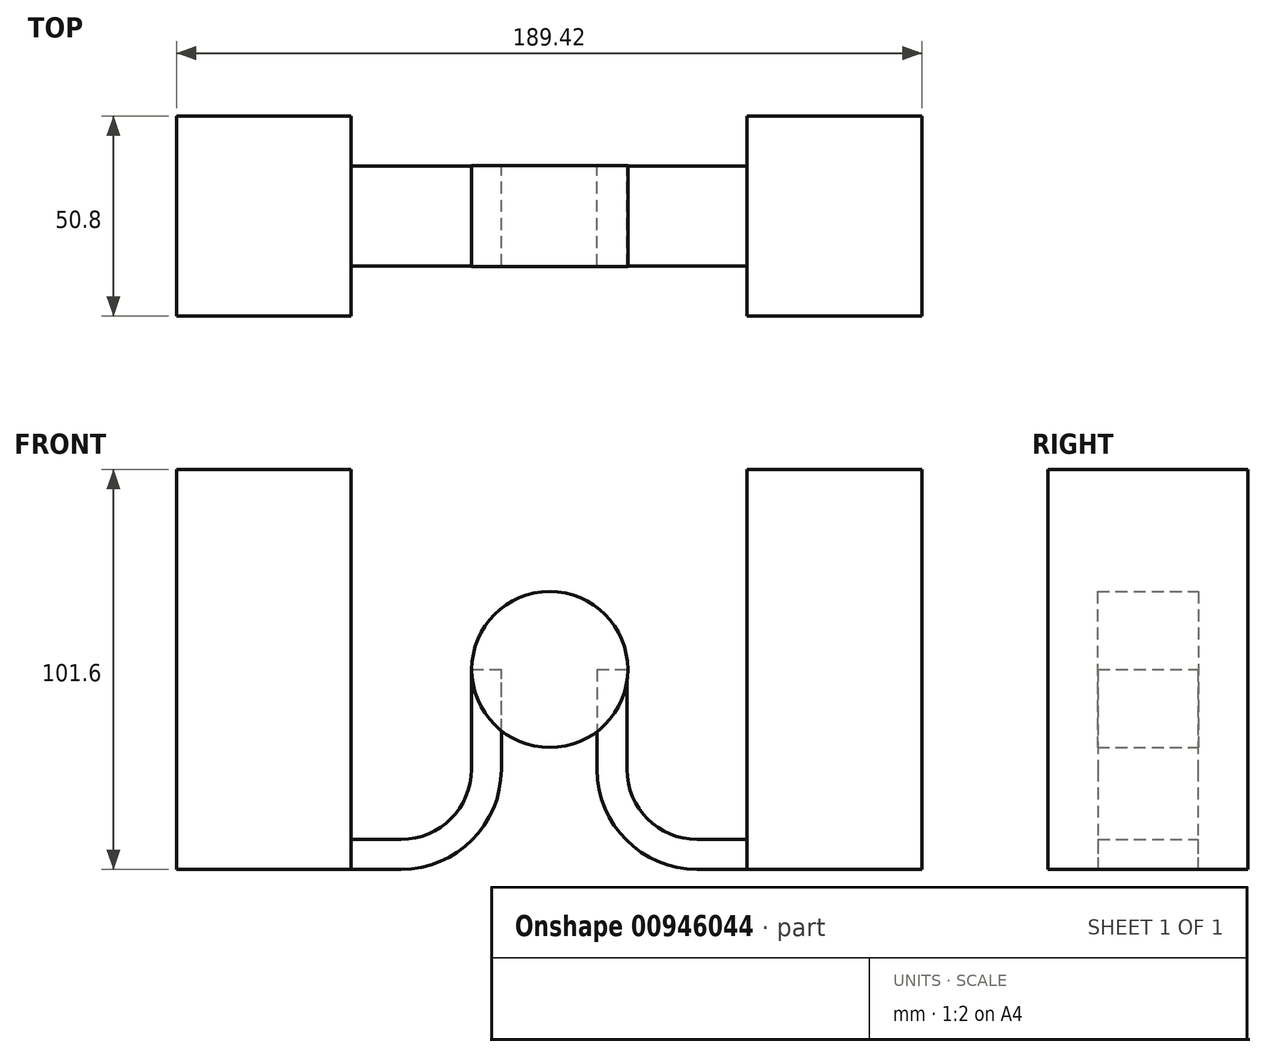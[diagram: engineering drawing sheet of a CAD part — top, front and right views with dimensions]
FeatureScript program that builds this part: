
annotation { "Feature Type Name" : "Feature", "Feature Type Description" : "" }
export const myFeature = defineFeature(function(context is Context, id is Id, definition is map)
    precondition{}
    {
        {
            var Q0;
            Q0=qCreatedBy(makeId("Front.planeOp"),FACE);
            var sketch = newSketch(context, id + "F0", { "sketchPlane" : qUnion([Q0])});
            skLineSegment(sketch, "E0.bottom", {"start": v(-94.87, 50.8) * mm, "end": v(-50.42, 50.8) * mm});
            skLineSegment(sketch, "E0.top", {"start": v(-94.87, -50.8) * mm, "end": v(-50.42, -50.8) * mm});
            skLineSegment(sketch, "E0.left", {"start": v(-94.87, 50.8) * mm, "end": v(-94.87, -50.8) * mm});
            skLineSegment(sketch, "E0.right", {"start": v(-50.42, 50.8) * mm, "end": v(-50.42, -50.8) * mm});
            skPoint(sketch, "E0.middle", {"position": v(-72.65, 0) * mm});
            skLineSegment(sketch, "E1.bottom", {"start": v(94.55, 50.8) * mm, "end": v(50.1, 50.8) * mm});
            skLineSegment(sketch, "E1.top", {"start": v(94.55, -50.8) * mm, "end": v(50.1, -50.8) * mm});
            skLineSegment(sketch, "E1.left", {"start": v(94.55, 50.8) * mm, "end": v(94.55, -50.8) * mm});
            skLineSegment(sketch, "E1.right", {"start": v(50.1, 50.8) * mm, "end": v(50.1, -50.8) * mm});
            skPoint(sketch, "E1.middle", {"position": v(72.32, 0) * mm});
            skLineSegment(sketch, "E2", {"start": v(-50.42, -50.8) * mm, "end": v(-37.72, -50.8) * mm});
            skLineSegment(sketch, "E3", {"start": v(50.1, -50.8) * mm, "end": v(37.4, -50.8) * mm});
            skArc(sketch, "E4", {"start": v(-37.72, -50.8) * mm, "mid": v(-19.76, -43.36) * mm, "end": v(-12.32, -25.4) * mm});
            skArc(sketch, "E5", {"start": v(37.4, -50.8) * mm, "mid": v(19.44, -43.36) * mm, "end": v(12, -25.4) * mm});
            skLineSegment(sketch, "E6", {"start": v(-12.32, -25.4) * mm, "end": v(-12.32, 0) * mm});
            skLineSegment(sketch, "E7", {"start": v(12, 0) * mm, "end": v(12, -25.4) * mm});
            skLineSegment(sketch, "E8.0", {"start": v(-19.94, -25.4) * mm, "end": v(-19.94, 0) * mm});
            skArc(sketch, "E8.1", {"start": v(-37.72, -43.18) * mm, "mid": v(-25.15, -37.97) * mm, "end": v(-19.94, -25.4) * mm});
            skLineSegment(sketch, "E8.2", {"start": v(-50.42, -43.18) * mm, "end": v(-37.72, -43.18) * mm});
            skLineSegment(sketch, "E9.0", {"start": v(19.62, 0) * mm, "end": v(19.62, -25.4) * mm});
            skArc(sketch, "E9.1", {"start": v(37.4, -43.18) * mm, "mid": v(24.83, -37.97) * mm, "end": v(19.62, -25.4) * mm});
            skLineSegment(sketch, "E9.2", {"start": v(50.1, -43.18) * mm, "end": v(37.4, -43.18) * mm});
            skLineSegment(sketch, "E10", {"start": v(-19.94, 0) * mm, "end": v(-12.32, 0) * mm});
            skLineSegment(sketch, "E11", {"start": v(12, 0) * mm, "end": v(19.62, 0) * mm});
            skSolve(sketch);
        }
        {
            var Q0;
            {var subQ1=sQuery(id+"F0.wireOp",EDGE,"E0.bottom");Q0=makeQuery(id+"F0.imprint","IMPRINT",FACE,{"disambiguationData":[TD([[makeQuery(id+"F0.imprint","IMPRINT",EDGE,{"derivedFrom":subQ1}),-1.0]])]});}
            var Q1;
            {var subQ1=sQuery(id+"F0.wireOp",EDGE,"E1.bottom");Q1=makeQuery(id+"F0.imprint","IMPRINT",FACE,{"disambiguationData":[TD([[makeQuery(id+"F0.imprint","IMPRINT",EDGE,{"derivedFrom":subQ1}),1.0]])]});}
            extrude(context, id + "F1", {"entities" : qUnion([Q0, Q1]), "endBound" : BoundingType.SYMMETRIC, "depth" : 50.8 * mm, "offsetDistance" : 25.4 * mm});
        }
        {
            var Q0;
            {var subQ0=sQuery(id+"F0.wireOp",EDGE,"E2");Q0=makeQuery(id+"F0.imprint","IMPRINT",FACE,{"disambiguationData":[TD([[makeQuery(id+"F0.imprint","IMPRINT",EDGE,{"derivedFrom":subQ0}),1.0]])]});}
            var Q1;
            {var subQ0=sQuery(id+"F0.wireOp",EDGE,"E3");Q1=makeQuery(id+"F0.imprint","IMPRINT",FACE,{"disambiguationData":[TD([[makeQuery(id+"F0.imprint","IMPRINT",EDGE,{"derivedFrom":subQ0}),-1.0]])]});}
            extrude(context, id + "F2", {"entities" : qUnion([Q0, Q1]), "endBound" : BoundingType.SYMMETRIC, "depth" : 25.4 * mm, "offsetDistance" : 25.4 * mm});
        }
        {
            var Q0;
            Q0=qCreatedBy(makeId("Top.planeOp"),FACE);
            var sketch = newSketch(context, id + "F3", { "sketchPlane" : qUnion([Q0])});
            skLineSegment(sketch, "E12.bottom", {"start": v(-19.83, 12.79) * mm, "end": v(19.83, 12.79) * mm});
            skLineSegment(sketch, "E12.top", {"start": v(-19.83, -12.79) * mm, "end": v(19.83, -12.79) * mm});
            skLineSegment(sketch, "E12.left", {"start": v(-19.83, 12.79) * mm, "end": v(-19.83, -12.79) * mm});
            skLineSegment(sketch, "E12.right", {"start": v(19.83, 12.79) * mm, "end": v(19.83, -12.79) * mm});
            skPoint(sketch, "E12.middle", {"position": v(0, 0) * mm});
            skLineSegment(sketch, "E13", {"start": v(0, 12.79) * mm, "end": v(0, -12.79) * mm});
            skSolve(sketch);
        }
        {
            var Q0;
            {var subQ0=sQuery(id+"F3.wireOp",EDGE,"E12.right");Q0=makeQuery(id+"F3.imprint","IMPRINT",FACE,{"disambiguationData":[TD([[makeQuery(id+"F3.imprint","IMPRINT",EDGE,{"derivedFrom":subQ0}),-1.0]])]});}
            var Q1;
            Q1=sQuery(id+"F3.wireOp",EDGE,"E13");
            revolve(context, id + "F4", {"surfaceOperationType" : NewSurfaceOperationType.NEW, "entities" : qUnion([Q0]), "axis" : qUnion([Q1]), "revolveType" : RevolveType.FULL});
        }
    });
